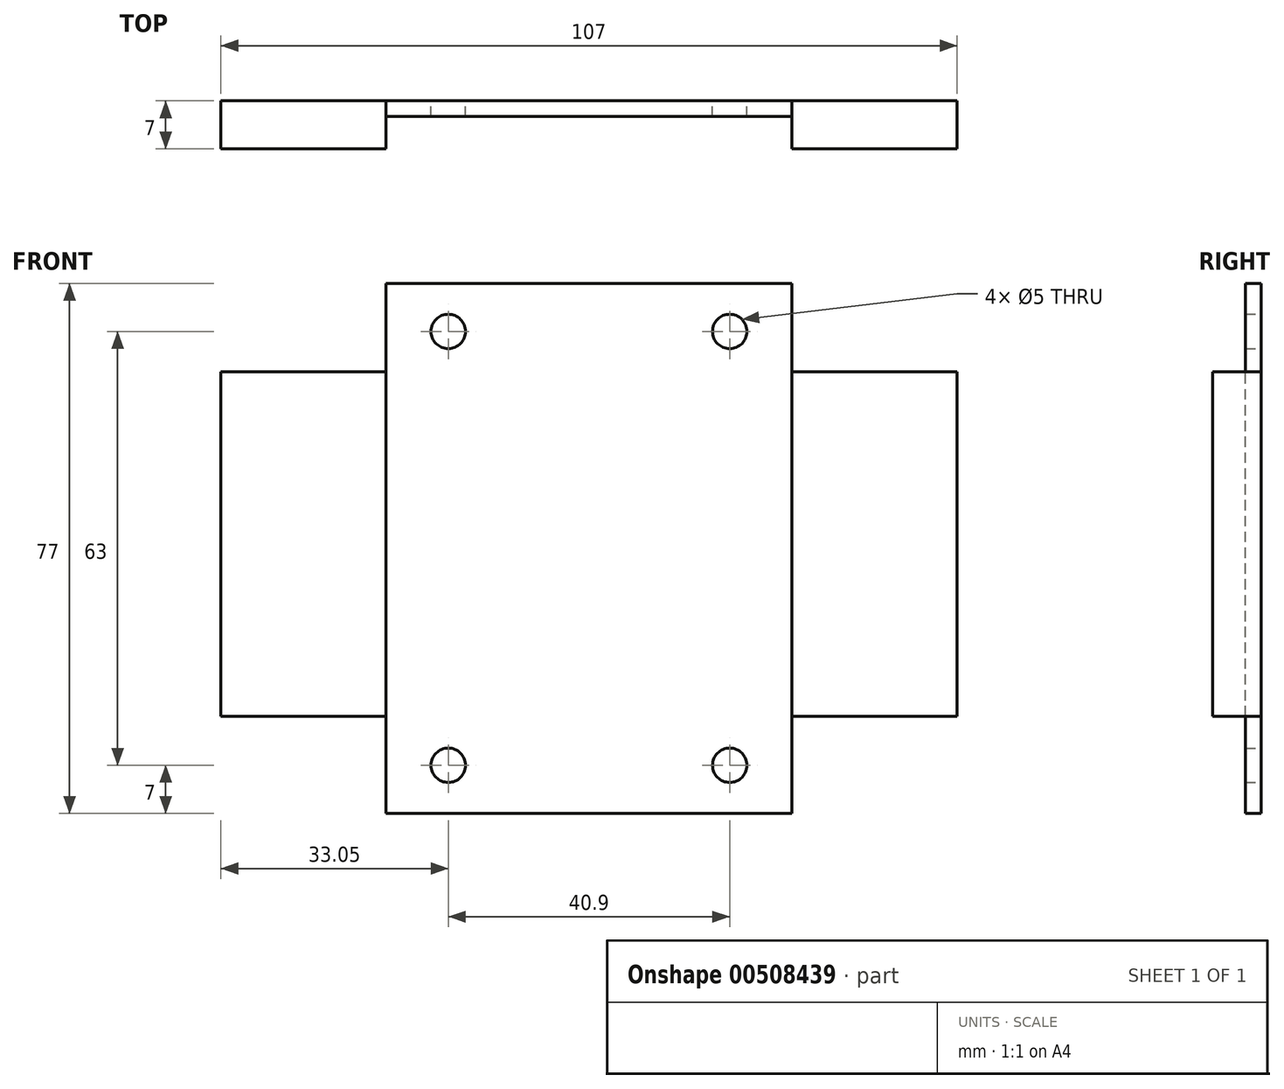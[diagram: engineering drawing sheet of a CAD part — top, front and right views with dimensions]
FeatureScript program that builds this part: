
annotation { "Feature Type Name" : "Feature", "Feature Type Description" : "" }
export const myFeature = defineFeature(function(context is Context, id is Id, definition is map)
    precondition{}
    {
        {
            var Q0;
            Q0=qCreatedBy(makeId("Front.planeOp"),FACE);
            var sketch = newSketch(context, id + "F0", { "sketchPlane" : qUnion([Q0])});
            skLineSegment(sketch, "E0.bottom", {"start": v(29.5, -38.5) * mm, "end": v(-29.5, -38.5) * mm});
            skLineSegment(sketch, "E0.top", {"start": v(29.5, 38.5) * mm, "end": v(-29.5, 38.5) * mm});
            skLineSegment(sketch, "E0.left", {"start": v(29.5, -38.5) * mm, "end": v(29.5, 38.5) * mm});
            skLineSegment(sketch, "E0.right", {"start": v(-29.5, -38.5) * mm, "end": v(-29.5, 38.5) * mm});
            skPoint(sketch, "E0.middle", {"position": v(0, 0) * mm});
            skCircle(sketch, "E1", {"center": v(-20.45, 31.5) * mm, "radius": 2.5 * mm});
            skLineSegment(sketch, "E2", {"start": v(-20.45, 31.5) * mm, "end": v(0, 31.5) * mm, "construction": true});
            skLineSegment(sketch, "E3", {"start": v(-20.45, 31.5) * mm, "end": v(-20.45, 0) * mm, "construction": true});
            skCircle(sketch, "E4.MirrorC", {"center": v(20.45, 31.5) * mm, "radius": 2.5 * mm});
            skCircle(sketch, "E5.MirrorC", {"center": v(-20.45, -31.5) * mm, "radius": 2.5 * mm});
            skCircle(sketch, "E6.MirrorC", {"center": v(20.45, -31.5) * mm, "radius": 2.5 * mm});
            skLineSegment(sketch, "E7.bottom", {"start": v(29.5, 25.62) * mm, "end": v(53.5, 25.62) * mm});
            skLineSegment(sketch, "E7.top", {"start": v(29.5, -24.38) * mm, "end": v(53.5, -24.38) * mm});
            skLineSegment(sketch, "E7.left", {"start": v(29.5, 25.62) * mm, "end": v(29.5, -24.38) * mm});
            skLineSegment(sketch, "E7.right", {"start": v(53.5, 25.62) * mm, "end": v(53.5, -24.38) * mm});
            skLineSegment(sketch, "E8.MirrorCS", {"start": v(-29.5, -24.38) * mm, "end": v(-53.5, -24.38) * mm});
            skLineSegment(sketch, "E9.MirrorCS", {"start": v(-53.5, 25.62) * mm, "end": v(-53.5, -24.38) * mm});
            skLineSegment(sketch, "E10.MirrorCS", {"start": v(-29.5, 25.62) * mm, "end": v(-53.5, 25.62) * mm});
            skSolve(sketch);
        }
        {
            var Q0;
            {var subQ4=sQuery(id+"F0.wireOp",EDGE,"E0.bottom");Q0=makeQuery(id+"F0.imprint","IMPRINT",FACE,{"disambiguationData":[TD([[makeQuery(id+"F0.imprint","IMPRINT",EDGE,{"derivedFrom":subQ4}),-1.0]])]});}
            extrude(context, id + "F1", {"entities" : qUnion([Q0]), "depth" : 2.3 * mm, "offsetDistance" : 25 * mm});
        }
        {
            var Q0;
            Q0=makeQuery(id+"F0.imprint","IMPRINT",FACE,{"disambiguationData":[TD([[makeQuery(id+"F0.imprint","IMPRINT",EDGE,{"derivedFrom":sQuery(id+"F0.wireOp",EDGE,"E7.bottom")}),-1.0]])]});
            var Q1;
            {var subQ0=sQuery(id+"F0.wireOp",EDGE,"E8.MirrorCS");Q1=makeQuery(id+"F0.imprint","IMPRINT",FACE,{"disambiguationData":[TD([[makeQuery(id+"F0.imprint","IMPRINT",EDGE,{"derivedFrom":subQ0}),-1.0]])]});}
            extrude(context, id + "F2", {"entities" : qUnion([Q0, Q1]), "operationType" : NewBodyOperationType.ADD, "depth" : 7 * mm, "offsetDistance" : 25 * mm});
        }
    });
